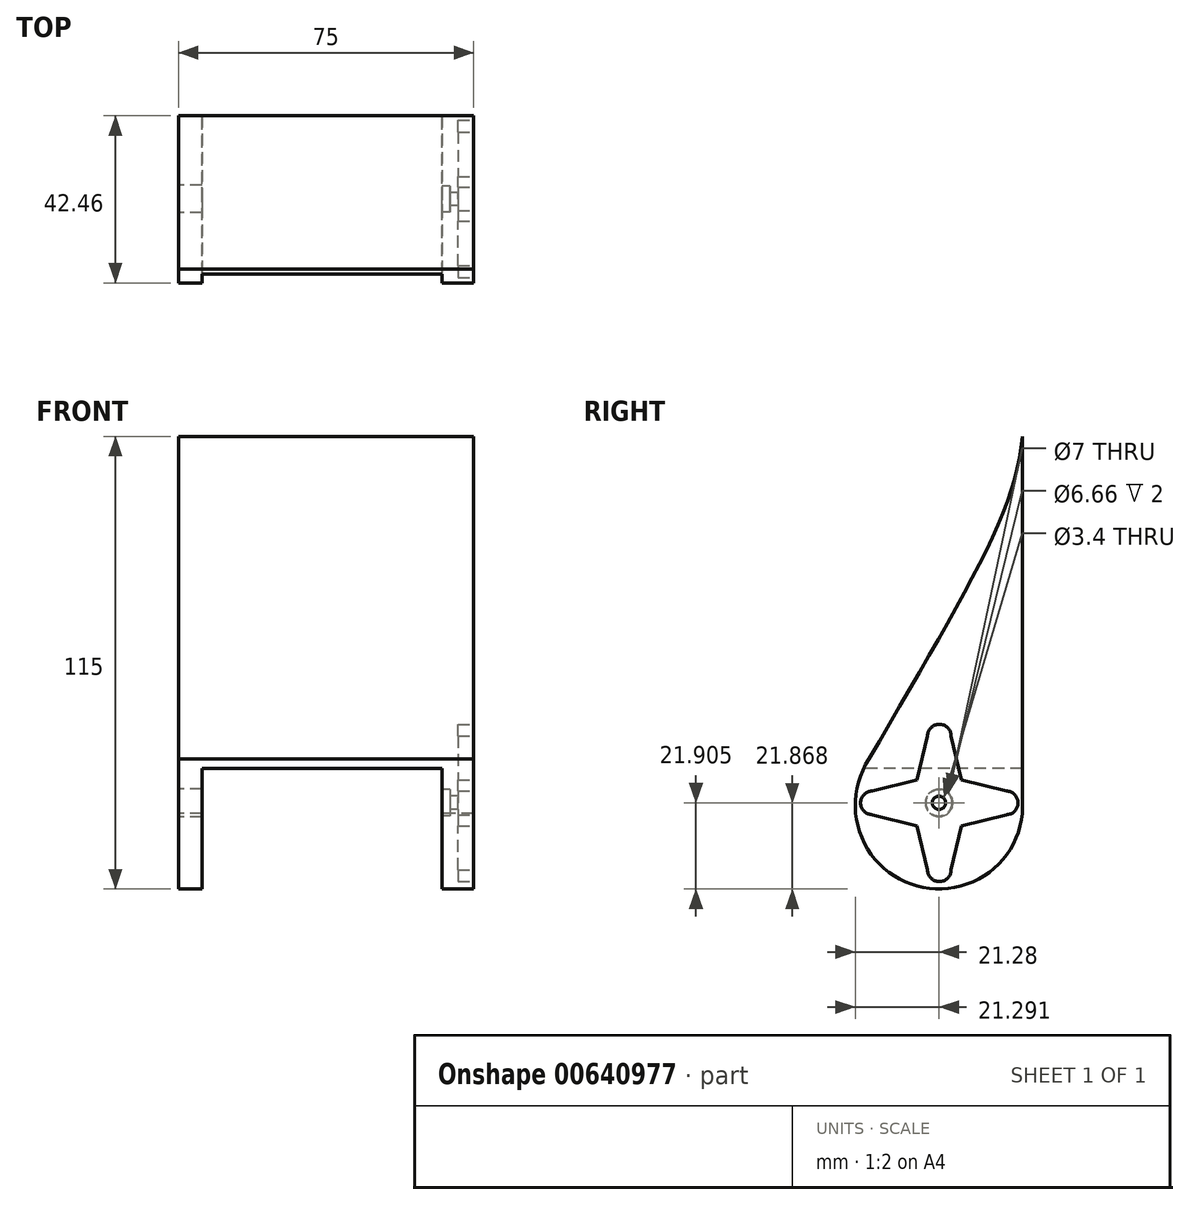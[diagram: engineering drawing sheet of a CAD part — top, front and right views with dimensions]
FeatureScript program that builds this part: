
annotation { "Feature Type Name" : "Feature", "Feature Type Description" : "" }
export const myFeature = defineFeature(function(context is Context, id is Id, definition is map)
    precondition{}
    {
        {
            var Q0;
            Q0=qCreatedBy(makeId("Right.planeOp"),FACE);
            var sketch = newSketch(context, id + "F0", { "sketchPlane" : qUnion([Q0])});
            skArc(sketch, "E0", {"start": v(-17.78, -27.31) * mm, "mid": v(-7.1, -59.07) * mm, "end": v(21.18, -41.11) * mm});
            skLineSegment(sketch, "E1", {"start": v(21.18, -41.11) * mm, "end": v(21.18, 54.7) * mm});
            skFitSpline(sketch, "E2", {"points": [v(21.18, 54.7) * mm, v(13.28, 28.42) * mm, v(-19.01, -29.44) * mm], "startDerivative": vector(-6.75, -66.5) * mm, "endDerivative": vector(-61.13, -105.91) * mm});
            skLineSegment(sketch, "E3", {"start": v(21.18, 54.7) * mm, "end": v(0, -60.3) * mm, "construction": true});
            skLineSegment(sketch, "E4", {"start": v(0, -60.3) * mm, "end": v(59.1, -60.3) * mm, "construction": true});
            skLineSegment(sketch, "E5", {"start": v(59.1, -60.3) * mm, "end": v(59.1, 54.7) * mm, "construction": true});
            skSolve(sketch);
        }
        {
            var Q0;
            Q0 = qSketchRegion(id + "F0", true);
            extrude(context, id + "F1", {"entities" : qUnion([Q0]), "depth" : 75 * mm, "offsetDistance" : 25.4 * mm});
        }
        {
            var Q0;
            Q0=makeQuery(id+"F1.opExtrude","CAP_FACE",FACE,{"disambiguationData":[OSD([sQuery(id+"F0.wireOp",EDGE,"E0"),sQuery(id+"F0.wireOp",EDGE,"E1"),sQuery(id+"F0.wireOp",EDGE,"E2")])],"isStart":false});
            var sketch = newSketch(context, id + "F2", { "sketchPlane" : qUnion([Q0])});
            skLineSegment(sketch, "E6", {"start": v(35.97, -38.58) * mm, "end": v(-34.92, -38.58) * mm, "construction": true});
            skLineSegment(sketch, "E7.MirrorCS", {"start": v(4.4, -38.43) * mm, "end": v(4.38, -38.58) * mm});
            skLineSegment(sketch, "E8.MirrorCS", {"start": v(-4.6, -38.43) * mm, "end": v(-4.57, -38.58) * mm});
            skArc(sketch, "E9", {"start": v(17.08, -41.43) * mm, "mid": v(20.08, -38.43) * mm, "end": v(17.08, -35.43) * mm});
            skArc(sketch, "E10.MirrorC", {"start": v(-16.92, -41.43) * mm, "mid": v(-19.92, -38.43) * mm, "end": v(-16.92, -35.43) * mm});
            skArc(sketch, "E11", {"start": v(3.08, -21.43) * mm, "mid": v(0.08, -18.43) * mm, "end": v(-2.92, -21.43) * mm});
            skArc(sketch, "E12.MirrorC", {"start": v(3.08, -55.43) * mm, "mid": v(0.08, -58.43) * mm, "end": v(-2.92, -55.43) * mm});
            skLineSegment(sketch, "E13", {"start": v(-16.92, -41.43) * mm, "end": v(-5.56, -44.25) * mm});
            skLineSegment(sketch, "E14.MirrorCS", {"start": v(-16.92, -35.43) * mm, "end": v(-5.56, -32.62) * mm});
            skLineSegment(sketch, "E15.MirrorCS", {"start": v(17.08, -35.43) * mm, "end": v(5.72, -32.62) * mm});
            skLineSegment(sketch, "E16.MirrorCS", {"start": v(17.08, -41.43) * mm, "end": v(5.72, -44.25) * mm});
            skLineSegment(sketch, "E17", {"start": v(-2.92, -21.43) * mm, "end": v(-5.56, -32.62) * mm});
            skLineSegment(sketch, "E18.MirrorCS", {"start": v(3.08, -21.43) * mm, "end": v(5.72, -32.62) * mm});
            skLineSegment(sketch, "E19.MirrorCS", {"start": v(-2.92, -55.43) * mm, "end": v(-5.56, -44.25) * mm});
            skLineSegment(sketch, "E20.MirrorCS", {"start": v(3.08, -55.43) * mm, "end": v(5.72, -44.25) * mm});
            skCircle(sketch, "E21", {"center": v(0.01, -38.43) * mm, "radius": 15.6 * mm, "construction": true});
            skLineSegment(sketch, "E22", {"start": v(-0.1, -22.83) * mm, "end": v(-0.1, -54.03) * mm, "construction": true});
            skSolve(sketch);
        }
        {
            var Q0;
            Q0=makeQuery(id+"F2.imprint","IMPRINT",FACE,{"disambiguationData":[TD([[makeQuery(id+"F2.imprint","IMPRINT",EDGE,{"derivedFrom":sQuery(id+"F2.wireOp",EDGE,"E9")}),1.0]])]});
            extrude(context, id + "F3", {"entities" : qUnion([Q0]), "operationType" : NewBodyOperationType.REMOVE, "oppositeDirection" : true, "depth" : 4 * mm, "offsetDistance" : 25.4 * mm});
        }
        {
            var Q0;
            Q0=qCreatedBy(makeId("Right.planeOp"),FACE);
            cPlane(context, id + "F4", {"entities" : qUnion([Q0]), "cplaneType" : CPlaneType.OFFSET, "offset" : 50 * mm, "width" : 152.4 * mm, "height" : 152.4 * mm});
        }
        {
            var Q0;
            Q0=qCreatedBy(id+"F4.planeOp",FACE);
            var sketch = newSketch(context, id + "F5", { "sketchPlane" : qUnion([Q0])});
            skLineSegment(sketch, "E23.bottom", {"start": v(30.96, -29.64) * mm, "end": v(-30.96, -29.64) * mm});
            skLineSegment(sketch, "E23.top", {"start": v(30.96, -67.29) * mm, "end": v(-30.96, -67.29) * mm});
            skLineSegment(sketch, "E23.left", {"start": v(30.96, -29.64) * mm, "end": v(30.96, -67.29) * mm});
            skLineSegment(sketch, "E23.right", {"start": v(-30.96, -29.64) * mm, "end": v(-30.96, -67.29) * mm});
            skCircle(sketch, "E24", {"center": v(0, -38.46) * mm, "radius": 17.93 * mm, "construction": true});
            skSolve(sketch);
        }
        {
            var Q0;
            Q0=makeQuery(id+"F5.imprint","IMPRINT",FACE,{"disambiguationData":[TD([[makeQuery(id+"F5.imprint","IMPRINT",EDGE,{"derivedFrom":sQuery(id+"F5.wireOp",EDGE,"E23.bottom")}),1.0]])]});
            extrude(context, id + "F6", {"entities" : qUnion([Q0]), "operationType" : NewBodyOperationType.REMOVE, "depth" : 17 * mm, "offsetDistance" : 25.4 * mm});
        }
        {
            var Q0;
            Q0 = qSketchRegion(id + "F5", true);
            extrude(context, id + "F7", {"entities" : qUnion([Q0]), "operationType" : NewBodyOperationType.REMOVE, "oppositeDirection" : true, "depth" : 44 * mm, "offsetDistance" : 25.4 * mm});
        }
        {
            var Q0;
            Q0=makeQuery(id+"F1.opExtrude","CAP_FACE",FACE,{"disambiguationData":[OSD([sQuery(id+"F0.wireOp",EDGE,"E0"),sQuery(id+"F0.wireOp",EDGE,"E1"),sQuery(id+"F0.wireOp",EDGE,"E2")])],"isStart":true});
            var sketch = newSketch(context, id + "F8", { "sketchPlane" : qUnion([Q0])});
            skPoint(sketch, "E25", {"position": v(-0.01, -38.43) * mm});
            skSolve(sketch);
        }
        {
            var Q0;
            Q0=sQuery(id+"F8.wireOp",VERTEX,"E25");
            var Q1;
            Q1=makeQuery(id+"F1.opExtrude","SWEPT_BODY",BODY,{"disambiguationData":[OSD([sQuery(id+"F0.wireOp",EDGE,"E0"),sQuery(id+"F0.wireOp",EDGE,"E1"),sQuery(id+"F0.wireOp",EDGE,"E2")])]});
            hole(context, id + "F9", {"style" : HoleStyle.SIMPLE, "endStyle" : HoleEndStyle.BLIND, "holeDiameter" : 7 * mm, "majorDiameter" : 6.35 * mm, "holeDepth" : 15 * mm, "isTappedThrough" : true, "tappedDepth" : 12.7 * mm, "tapClearance" : 3, "locations" : qUnion([Q0]), "scope" : qUnion([Q1])});
        }
        {
            var Q0;
            Q0=makeQuery(id+"F6.boolean.opBoolean","COPY",FACE,{"derivedFrom":makeQuery(id+"F6.opExtrude","CAP_FACE",FACE,{"disambiguationData":[OSD([sQuery(id+"F5.wireOp",EDGE,"E23.bottom"),sQuery(id+"F5.wireOp",EDGE,"E23.top"),sQuery(id+"F5.wireOp",EDGE,"E23.left"),sQuery(id+"F5.wireOp",EDGE,"E23.right")])],"isStart":false})});
            var sketch = newSketch(context, id + "F10", { "sketchPlane" : qUnion([Q0])});
            skCircle(sketch, "E26", {"center": v(0, -38.4) * mm, "radius": 3.33 * mm});
            skCircle(sketch, "E27", {"center": v(0, -38.4) * mm, "radius": 1.7 * mm});
            skSolve(sketch);
        }
        {
            var Q0;
            Q0 = qSketchRegion(id + "F10", true);
            extrude(context, id + "F11", {"entities" : qUnion([Q0]), "operationType" : NewBodyOperationType.REMOVE, "oppositeDirection" : true, "depth" : 2 * mm, "offsetDistance" : 25.4 * mm});
        }
        {
            var Q0;
            Q0=makeQuery(id+"F10.imprint","IMPRINT",FACE,{"disambiguationData":[TD([[makeQuery(id+"F10.imprint","IMPRINT",EDGE,{"derivedFrom":sQuery(id+"F10.wireOp",EDGE,"E27")}),1.0]])]});
            extrude(context, id + "F12", {"entities" : qUnion([Q0]), "operationType" : NewBodyOperationType.REMOVE, "oppositeDirection" : true, "depth" : 25.4 * mm, "offsetDistance" : 25.4 * mm});
        }
    });
